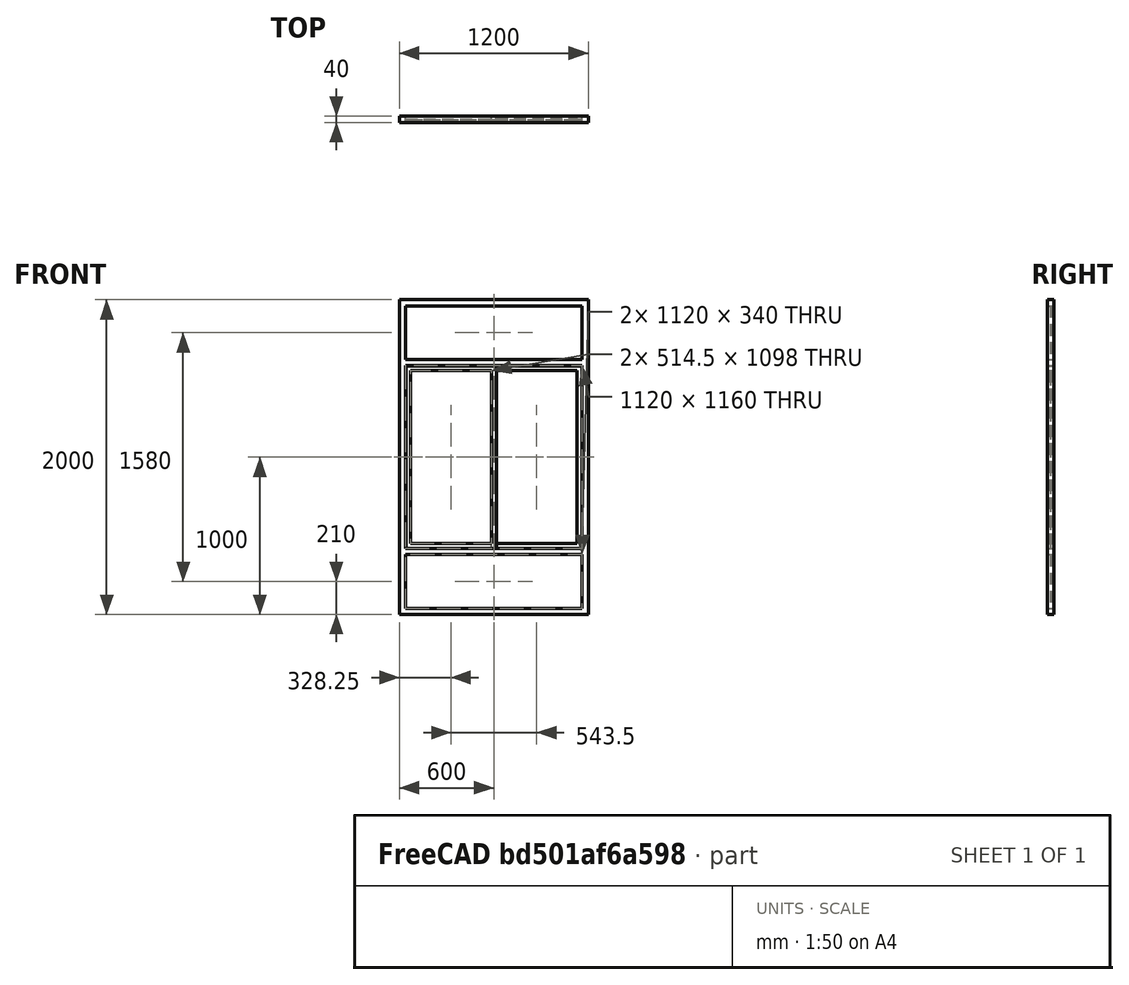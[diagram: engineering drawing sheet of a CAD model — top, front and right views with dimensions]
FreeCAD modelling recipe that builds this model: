
FCSTD DOCUMENT  (FreeCAD 0.16R6704 (Git))
Label: Sliding window and two fixed vertical sheets
License: CreativeCommons Attribution
LicenseURL: http://creativecommons.org/licenses/by/4.0/
objects: Sketcher::SketchObject×1, Part::FeaturePython×1
note: 2 computed .brp shape members not serialized (recipe doc carries the construction recipe); baked Part::Feature solids carry a one-line shape summary decoded from their .brp

FEATURE [Sketcher::SketchObject] Sketch116  label="Esboço caixilho correr 3"
  Placement = pos=(0,0,0) rot=(1,0,0;1.5708rad)
  sketch-geometry (35):
    g0: LineSegment StartX=1200 StartY=2000 StartZ=0 EndX=0 EndY=2000 EndZ=0
    g1: LineSegment StartX=0 StartY=2000 StartZ=0 EndX=0 EndY=0 EndZ=0
    g2: LineSegment StartX=0 StartY=0 StartZ=0 EndX=1200 EndY=0 EndZ=0
    g3: LineSegment StartX=1200 StartY=0 StartZ=0 EndX=1200 EndY=2000 EndZ=0
    g4: LineSegment StartX=40 StartY=380 StartZ=0 EndX=1160 EndY=380 EndZ=0
    g5: LineSegment StartX=1160 StartY=380 StartZ=0 EndX=1160 EndY=40 EndZ=0
    g6: LineSegment StartX=1160 StartY=40 StartZ=0 EndX=40 EndY=40 EndZ=0
    g7: LineSegment StartX=40 StartY=40 StartZ=0 EndX=40 EndY=380 EndZ=0
    g8: LineSegment StartX=40 StartY=1960 StartZ=0 EndX=1160 EndY=1960 EndZ=0
    g9: LineSegment StartX=1160 StartY=1960 StartZ=0 EndX=1160 EndY=1620 EndZ=0
    g10: LineSegment StartX=1160 StartY=1620 StartZ=0 EndX=40 EndY=1620 EndZ=0
    g11: LineSegment StartX=40 StartY=1620 StartZ=0 EndX=40 EndY=1960 EndZ=0
    g12: LineSegment StartX=40 StartY=420 StartZ=0 EndX=1160 EndY=420 EndZ=0
    g13: LineSegment StartX=1160 StartY=420 StartZ=0 EndX=1160 EndY=1580 EndZ=0
    g14: LineSegment StartX=1160 StartY=1580 StartZ=0 EndX=40 EndY=1580 EndZ=0
    g15: LineSegment StartX=40 StartY=1580 StartZ=0 EndX=40 EndY=420 EndZ=0
    g16: LineSegment [constr] StartX=-293.085 StartY=1600 StartZ=0 EndX=1289.05 EndY=1600 EndZ=0
    g17: LineSegment [constr] StartX=-323.652 StartY=400 StartZ=0 EndX=1257.75 EndY=400 EndZ=0
    g18: LineSegment StartX=41 StartY=1579 StartZ=0 EndX=615.5 EndY=1579 EndZ=0
    g19: LineSegment StartX=615.5 StartY=1579 StartZ=0 EndX=615.5 EndY=421 EndZ=0
    g20: LineSegment StartX=615.5 StartY=421 StartZ=0 EndX=41 EndY=421 EndZ=0
    g21: LineSegment StartX=41 StartY=421 StartZ=0 EndX=41 EndY=1579 EndZ=0
    g22: LineSegment StartX=71 StartY=1549 StartZ=0 EndX=585.5 EndY=1549 EndZ=0
    g23: LineSegment StartX=585.5 StartY=1549 StartZ=0 EndX=585.5 EndY=451 EndZ=0
    g24: LineSegment StartX=585.5 StartY=451 StartZ=0 EndX=71 EndY=451 EndZ=0
    g25: LineSegment StartX=71 StartY=451 StartZ=0 EndX=71 EndY=1549 EndZ=0
    g26: LineSegment StartX=584.5 StartY=1579 StartZ=0 EndX=1159 EndY=1579 EndZ=0
    g27: LineSegment StartX=1159 StartY=1579 StartZ=0 EndX=1159 EndY=421 EndZ=0
    g28: LineSegment StartX=1159 StartY=421 StartZ=0 EndX=584.5 EndY=421 EndZ=0
    g29: LineSegment StartX=584.5 StartY=421 StartZ=0 EndX=584.5 EndY=1579 EndZ=0
    g30: LineSegment StartX=614.5 StartY=1549 StartZ=0 EndX=1129 EndY=1549 EndZ=0
    g31: LineSegment StartX=1129 StartY=1549 StartZ=0 EndX=1129 EndY=451 EndZ=0
    g32: LineSegment StartX=1129 StartY=451 StartZ=0 EndX=614.5 EndY=451 EndZ=0
    g33: LineSegment StartX=614.5 StartY=451 StartZ=0 EndX=614.5 EndY=1549 EndZ=0
    g34: LineSegment [constr] StartX=600 StartY=2144.9 StartZ=0 EndX=600 EndY=-330.098 EndZ=0
  constraints (98):
    c: Coincident(g0,g1)
    c: Horizontal(g0)
    c: Coincident(g1,g2)
    c: Vertical(g1)
    c: Coincident(g2,g3)
    c: Horizontal(g2)
    c: Coincident(g3,g0)
    c: Coincident(g4,g5)
    c: Horizontal(g4)
    c: Coincident(g5,g6)
    c: Vertical(g5)
    c: Coincident(g6,g7)
    c: Horizontal(g6)
    c: Coincident(g7,g4)
    c: Coincident(g8,g9)
    c: Horizontal(g8)
    c: Coincident(g9,g10)
    c: Vertical(g9)
    c: Coincident(g10,g11)
    c: Horizontal(g10)
    c: Coincident(g11,g8)
    c: Coincident(g12,g13)
    c: Horizontal(g12)
    c: Coincident(g13,g14)
    c: Vertical(g13)
    c: Coincident(g14,g15)
    c: Horizontal(g14)
    c: Coincident(g15,g12)
    c: DistanceX(g0,g8) = 40  'Montante esquerdo'
    c: DistanceY(g8,g0) = 40  'Montantel superior'
    c: DistanceX(g8,g0) = 40  'Montante direito'
    c: DistanceX(g10,g14) = 0
    c: DistanceX(g9,g13) = 0
    c: DistanceX(g12,g4) = 0
    c: DistanceX(g12,g4) = 0
    c: DistanceY(g14,g10) = 40  'Montante intermediário superior'
    c: DistanceY(g4,g12) = 40  'Montante intermediário inferior'
    c: DistanceX(g0,g0) = 1200  'Largura do vão'
    c: DistanceY(g2,g0) = 2000  'Altura do vão'
    c: Symmetric(g12,g4,g17)  'Constraint40'
    c: Symmetric(g14,g10,g16)
    c: DistanceY(g16,g0) = 400  'Altura parte superior'
    c: DistanceY(g2,g17) = 400  'Altura parte inferior'
    c: DistanceY(g1,g6) = 40  'Montante inferior'
    c: Coincident(g1,g-1)
    c: Vertical(g11)
    c: Vertical(g7)
    c: Vertical(g3)
    c: Vertical(g15)
    c: Coincident(g18,g19)
    c: Coincident(g19,g20)
    c: Coincident(g20,g21)
    c: Coincident(g21,g18)
    c: Horizontal(g18)
    c: Horizontal(g20)
    c: Vertical(g19)
    c: Vertical(g21)
    c: Coincident(g22,g23)
    c: Coincident(g23,g24)
    c: Coincident(g24,g25)
    c: Coincident(g25,g22)
    c: Horizontal(g22)
    c: Horizontal(g24)
    c: Vertical(g23)
    c: Vertical(g25)
    c: Coincident(g26,g27)
    c: Coincident(g27,g28)
    c: Coincident(g28,g29)
    c: Coincident(g29,g26)
    c: Horizontal(g26)
    c: Horizontal(g28)
    c: Vertical(g27)
    c: Vertical(g29)
    c: Coincident(g30,g31)
    c: Coincident(g31,g32)
    c: Coincident(g32,g33)
    c: Coincident(g33,g30)
    c: Horizontal(g30)
    c: Horizontal(g32)
    c: Vertical(g31)
    c: Vertical(g33)
    c: DistanceX(g18,g22) = 30  'Montante esquerdo folha 1'
    c: DistanceY(g22,g18) = 30  'Montantel superior folha 1'
    c: DistanceX(g22,g18) = 30  'Montante direito folha 1'
    c: DistanceY(g20,g24) = 30  'Montante inferior folha 1'
    c: DistanceX(g26,g30) = 30  'Montante esquerdo folha 2'
    c: DistanceX(g30,g26) = 30  'Montante direito folha 2'
    c: DistanceY(g30,g26) = 30  'Montante superior folha 2'
    c: DistanceY(g28,g32) = 30  'Montante inferior folha 2'
    c: DistanceX(g14,g18) = 1
    c: DistanceY(g18,g14) = 1
    c: DistanceY(g12,g20) = 1
    c: DistanceY(g26,g13) = 1
    c: DistanceX(g26,g13) = 1
    c: DistanceY(g12,g27) = 1
    c: DistanceX(g26,g22) = 1
    c: Symmetric(g18,g26,g34)
    c: Symmetric(g0,g0,g34)
FEATURE [Part::FeaturePython] Window084  label="Sliding window and two fixed vertical sheets"  # WARN: FeaturePython — macro-defined, semantics opaque (R4)
  Base = -> Sketch116
  Height = 0
  HoleDepth = 0
  MoveWithHost = true
  Normal = (0,1,0)
  Preset = 0
  Role = 0
  Width = 0
  WindowParts = MONTANTES | Frame | Wire0,Wire1,Wire2,Wire3,Wire4,Wire5,Wire6,Wire7 | 40.0 | 0.0 | MONTANTE 1 | Frame | Wire4,Wire5 | 20.0 | 0.0 | MONTANTE 2 | Frame | Wire6,Wire7 | 20.0 | 20.0 | VIDRO SUPERIOR | Glass panel | Wire2 | 4.0 | 18.0 | VIDRO INFERIOR | Glass panel | Wire1 | 4.0 | 18.0 | VIDRO 1 | Glass panel | Wire5 | 4.0 | 8.0 | VIDRO 2 | Glass panel | Wire7 | 4.0 | 28.0
